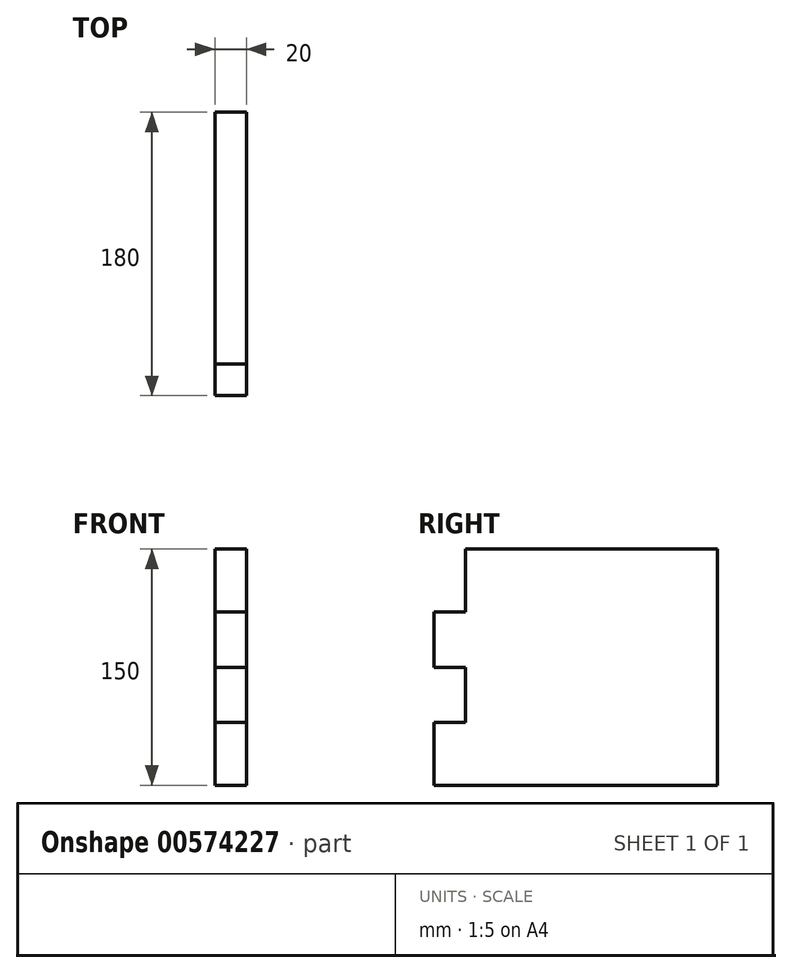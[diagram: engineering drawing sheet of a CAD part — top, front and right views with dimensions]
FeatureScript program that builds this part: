
annotation { "Feature Type Name" : "Feature", "Feature Type Description" : "" }
export const myFeature = defineFeature(function(context is Context, id is Id, definition is map)
    precondition{}
    {
        {
            var Q0;
            Q0=qCreatedBy(makeId("Right.planeOp"),FACE);
            var sketch = newSketch(context, id + "F0", { "sketchPlane" : qUnion([Q0])});
            skLineSegment(sketch, "E0.bottom", {"start": v(0, 0) * mm, "end": v(180, 0) * mm});
            skLineSegment(sketch, "E0.top", {"start": v(20, 150) * mm, "end": v(180, 150) * mm});
            skLineSegment(sketch, "E0.left", {"start": v(0, 0) * mm, "end": v(0, 40) * mm});
            skLineSegment(sketch, "E0.right", {"start": v(180, 0) * mm, "end": v(180, 150) * mm});
            skLineSegment(sketch, "E1", {"start": v(20, 150) * mm, "end": v(20, 110) * mm});
            skLineSegment(sketch, "E2", {"start": v(0, 75) * mm, "end": v(20, 75) * mm});
            skLineSegment(sketch, "E3", {"start": v(0, 110) * mm, "end": v(20, 110) * mm});
            skLineSegment(sketch, "E4", {"start": v(0, 40) * mm, "end": v(20, 40) * mm});
            skPoint(sketch, "E5.orphan", {"position": v(0, 150) * mm});
            skLineSegment(sketch, "E6.trimOffspring", {"start": v(0, 75) * mm, "end": v(0, 110) * mm});
            skLineSegment(sketch, "E7.trimOffspring", {"start": v(20, 75) * mm, "end": v(20, 40) * mm});
            skPoint(sketch, "E8.orphan", {"position": v(20, 0) * mm});
            skSolve(sketch);
        }
        {
            var Q0;
            Q0=makeQuery(id+"F0.imprint","IMPRINT",FACE,{"disambiguationData":[TD([[makeQuery(id+"F0.imprint","IMPRINT",EDGE,{"derivedFrom":sQuery(id+"F0.wireOp",EDGE,"E0.bottom")}),1.0]])]});
            extrude(context, id + "F1", {"entities" : qUnion([Q0]), "depth" : 20 * mm, "offsetDistance" : 25 * mm});
        }
    });
